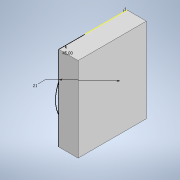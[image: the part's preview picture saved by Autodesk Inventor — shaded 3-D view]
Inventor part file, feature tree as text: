
AUTODESK INVENTOR PART (.ipt)
format: ipt  version: 2020 (Build 240168000, 168)  size: 172,544 bytes
history: native  units: mm
features: sketch x7, extrude x4, fillet x1
ambient origin geometry x8: Origin, YZ Plane, XZ Plane, XY Plane, X Axis, Y Axis, Z Axis, Center Point
bodies: Solid1 (feature_tree)
feature tree (12):
  extrude  "Extrusion1"  Depth=2.5mm
  extrude  "Extrusion4"  Depth=26.0mm
  sketch  "Sketch6"  dims[d11=21.0mm]
  extrude  "Extrusion2"  Depth=6.0mm
  extrude  "Extrusion3"  Depth=1.8mm
  fillet  "Fillet1"  Radius=1.1mm
  sketch  "Sketch5"  dims[d9=21.0mm d10=0.0mm]
  sketch  "Sketch2"  dims[d2=16.5mm d3=26.0mm]
  sketch  "Sketch1"  dims[d0=2.5mm d1=2.5mm]
  sketch  "Sketch3"  dims[d4=6.0mm d5=0.85mm]
  sketch  "Sketch4"  dims[d6=1.55mm d7=1.8mm d8=1.1mm]
  sketch  "Sketch7"  dims[d12=2.0mm d14=4.4mm d15=2.5mm d16=0.0mm d17=0.0mm d18=5.5mm d19=0.1mm d20=26.0mm d21=0.0mm d22=3.0mm d23=21.0mm d25=21.0mm d26=1.0mm d27=15.0mm d28=0.0mm d29=45.0deg]
